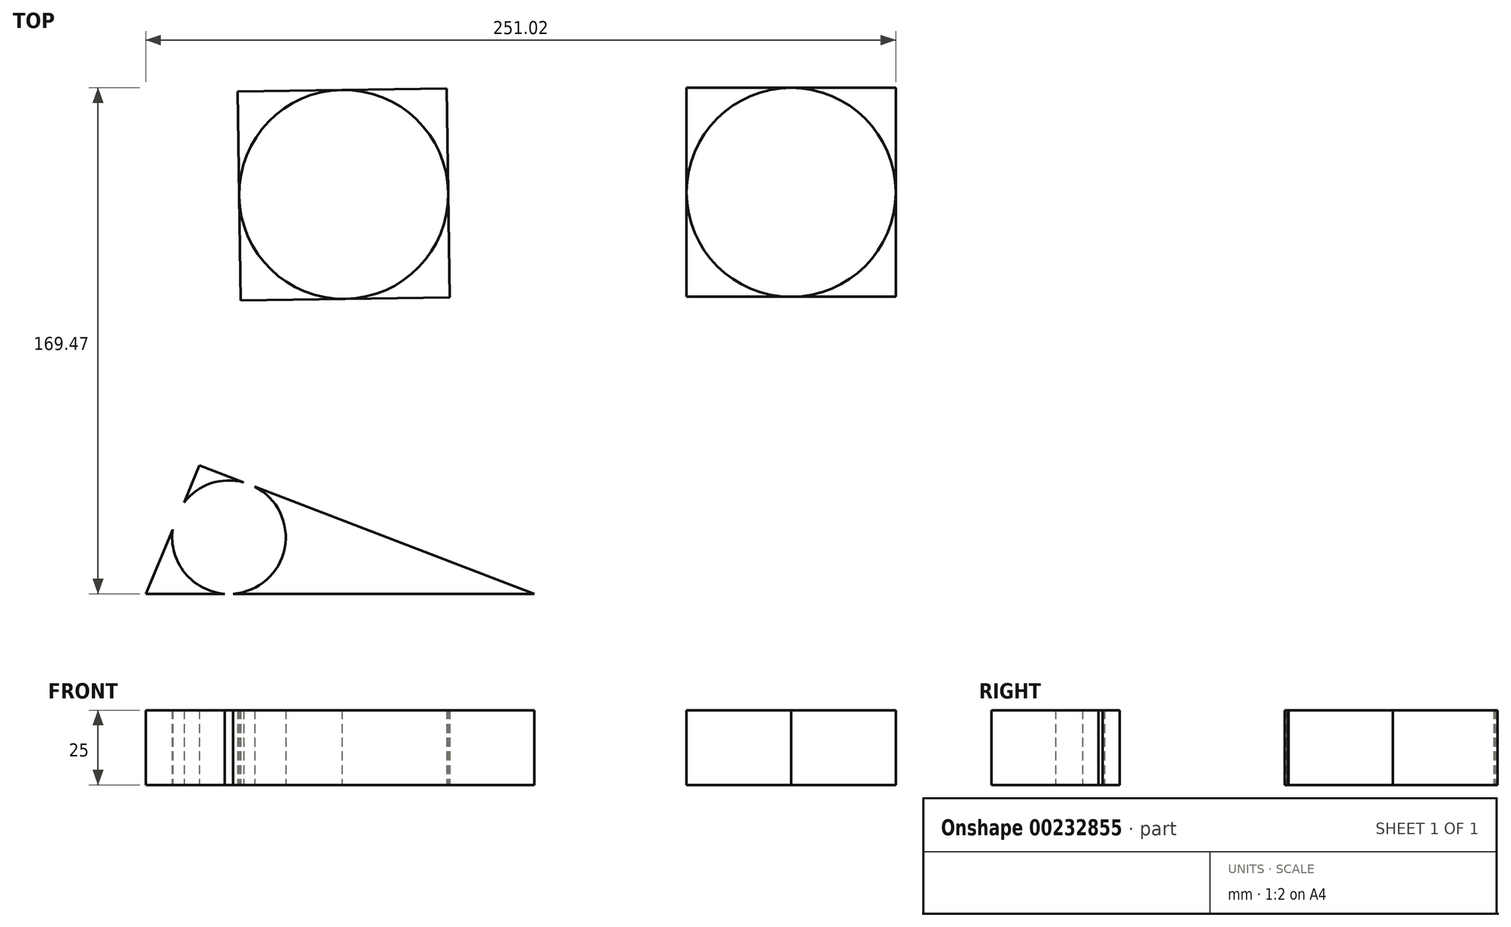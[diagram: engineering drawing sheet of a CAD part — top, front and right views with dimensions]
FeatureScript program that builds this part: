
annotation { "Feature Type Name" : "Feature", "Feature Type Description" : "" }
export const myFeature = defineFeature(function(context is Context, id is Id, definition is map)
    precondition{}
    {
        {
            var Q0;
            Q0=qCreatedBy(makeId("Top.planeOp"),FACE);
            var sketch = newSketch(context, id + "F0", { "sketchPlane" : qUnion([Q0])});
            skCircle(sketch, "E0", {"center": v(-236.28, 39.6) * mm, "radius": 35 * mm});
            skLineSegment(sketch, "E1", {"start": v(-200.74, 5.14) * mm, "end": v(-201.82, 75.14) * mm});
            skLineSegment(sketch, "E2", {"start": v(-201.82, 75.14) * mm, "end": v(-271.82, 74.06) * mm});
            skLineSegment(sketch, "E3", {"start": v(-271.82, 74.06) * mm, "end": v(-270.74, 4.07) * mm});
            skLineSegment(sketch, "E4", {"start": v(-270.74, 4.07) * mm, "end": v(-200.74, 5.14) * mm});
            skSolve(sketch);
        }
        {
            var Q0;
            {var subQ0=sQuery(id+"F0.wireOp",EDGE,"E3");Q0=makeQuery(id+"F0.imprint","IMPRINT",FACE,{"disambiguationData":[TD([[makeQuery(id+"F0.imprint","IMPRINT",EDGE,{"derivedFrom":subQ0}),1.0]])]});}
            var Q1;
            {var subQ0=sQuery(id+"F0.wireOp",EDGE,"E1");var subQ1=sQuery(id+"F0.wireOp",EDGE,"E0");var subQ2=makeQuery(id+"F0.imprint","INTERSECT",VERTEX,{"derivedFrom":[subQ1,subQ0]});Q1=makeQuery(id+"F0.imprint","IMPRINT",FACE,{"disambiguationData":[TD([[makeQuery(id+"F0.imprint","IMPRINT",EDGE,{"disambiguationData":[TD([[subQ2,-1.0]])],"derivedFrom":subQ1}),-1.0]])]});}
            extrude(context, id + "F1", {"entities" : qUnion([Q0, Q1]), "depth" : 25 * mm});
        }
        {
            var Q0;
            Q0=qCreatedBy(makeId("Top.planeOp"),FACE);
            var sketch = newSketch(context, id + "F2", { "sketchPlane" : qUnion([Q0])});
            skLineSegment(sketch, "E5", {"start": v(-121.49, 75.3) * mm, "end": v(-121.49, 5.3) * mm});
            skLineSegment(sketch, "E6", {"start": v(-121.49, 75.3) * mm, "end": v(-51.49, 75.3) * mm});
            skLineSegment(sketch, "E7", {"start": v(-51.49, 75.3) * mm, "end": v(-51.49, 5.3) * mm});
            skLineSegment(sketch, "E8", {"start": v(-51.49, 5.3) * mm, "end": v(-121.49, 5.3) * mm});
            skCircle(sketch, "E9", {"center": v(-86.49, 40.3) * mm, "radius": 35 * mm});
            skSolve(sketch);
        }
        {
            var Q0;
            {var subQ0=sQuery(id+"F2.wireOp",EDGE,"E6");var subQ1=sQuery(id+"F2.wireOp",EDGE,"E5");var subQ2=makeQuery(id+"F2.imprint","INTERSECT",VERTEX,{"derivedFrom":[subQ1,subQ0]});Q0=makeQuery(id+"F2.imprint","IMPRINT",FACE,{"disambiguationData":[TD([[makeQuery(id+"F2.imprint","IMPRINT",EDGE,{"disambiguationData":[TD([[subQ2,-1.0]])],"derivedFrom":subQ1}),1.0]])]});}
            var Q1;
            {var subQ0=sQuery(id+"F2.wireOp",EDGE,"E7");var subQ1=sQuery(id+"F2.wireOp",EDGE,"E6");var subQ2=makeQuery(id+"F2.imprint","INTERSECT",VERTEX,{"derivedFrom":[subQ1,subQ0]});Q1=makeQuery(id+"F2.imprint","IMPRINT",FACE,{"disambiguationData":[TD([[makeQuery(id+"F2.imprint","IMPRINT",EDGE,{"disambiguationData":[TD([[subQ2,1.0]])],"derivedFrom":subQ1}),-1.0]])]});}
            var Q2;
            {var subQ0=sQuery(id+"F2.wireOp",EDGE,"E8");var subQ1=sQuery(id+"F2.wireOp",EDGE,"E7");var subQ2=makeQuery(id+"F2.imprint","INTERSECT",VERTEX,{"derivedFrom":[subQ1,subQ0]});Q2=makeQuery(id+"F2.imprint","IMPRINT",FACE,{"disambiguationData":[TD([[makeQuery(id+"F2.imprint","IMPRINT",EDGE,{"disambiguationData":[TD([[subQ2,1.0]])],"derivedFrom":subQ1}),-1.0]])]});}
            var Q3;
            {var subQ0=sQuery(id+"F2.wireOp",EDGE,"E8");var subQ1=sQuery(id+"F2.wireOp",EDGE,"E5");var subQ2=makeQuery(id+"F2.imprint","INTERSECT",VERTEX,{"derivedFrom":[subQ1,subQ0]});Q3=makeQuery(id+"F2.imprint","IMPRINT",FACE,{"disambiguationData":[TD([[makeQuery(id+"F2.imprint","IMPRINT",EDGE,{"disambiguationData":[TD([[subQ2,1.0]])],"derivedFrom":subQ1}),1.0]])]});}
            extrude(context, id + "F3", {"entities" : qUnion([Q0, Q1, Q2, Q3]), "depth" : 25 * mm});
        }
        {
            var Q0;
            Q0=qCreatedBy(makeId("Top.planeOp"),FACE);
            var sketch = newSketch(context, id + "F4", { "sketchPlane" : qUnion([Q0])});
            skLineSegment(sketch, "E10", {"start": v(-302.51, -94.17) * mm, "end": v(-172.51, -94.17) * mm});
            skLineSegment(sketch, "E11", {"start": v(-172.51, -94.17) * mm, "end": v(-284.54, -51.17) * mm});
            skLineSegment(sketch, "E12", {"start": v(-284.54, -51.17) * mm, "end": v(-302.51, -94.17) * mm});
            skCircle(sketch, "E13", {"center": v(-274.69, -75.21) * mm, "radius": 19.01 * mm});
            skPoint(sketch, "E13.first.point", {"position": v(-266.12, -58.24) * mm});
            skPoint(sketch, "E13.second.point", {"position": v(-293.53, -72.67) * mm});
            skPoint(sketch, "E13.third.point", {"position": v(-273.3, -94.17) * mm});
            skSolve(sketch);
        }
        {
            var Q0;
            {var subQ0=sQuery(id+"F4.wireOp",EDGE,"E12");var subQ1=sQuery(id+"F4.wireOp",EDGE,"E10");var subQ2=makeQuery(id+"F4.imprint","INTERSECT",VERTEX,{"derivedFrom":[subQ1,subQ0]});Q0=makeQuery(id+"F4.imprint","IMPRINT",FACE,{"disambiguationData":[TD([[makeQuery(id+"F4.imprint","IMPRINT",EDGE,{"disambiguationData":[TD([[subQ2,-1.0]])],"derivedFrom":subQ1}),1.0]])]});}
            var Q1;
            {var subQ0=sQuery(id+"F4.wireOp",EDGE,"E13");var subQ1=sQuery(id+"F4.wireOp",EDGE,"E10");var subQ2=makeQuery(id+"F4.imprint","INTERSECT",VERTEX,{"disambiguationData":[OD(0.0)],"derivedFrom":[subQ1,subQ0]});Q1=makeQuery(id+"F4.imprint","IMPRINT",FACE,{"disambiguationData":[TD([[makeQuery(id+"F4.imprint","IMPRINT",EDGE,{"disambiguationData":[TD([[subQ2,-1.0]])],"derivedFrom":subQ1}),-1.0]])]});}
            var Q2;
            {var subQ0=sQuery(id+"F4.wireOp",EDGE,"E13");var subQ1=sQuery(id+"F4.wireOp",EDGE,"E11");var subQ2=makeQuery(id+"F4.imprint","INTERSECT",VERTEX,{"disambiguationData":[OD(0.0)],"derivedFrom":[subQ1,subQ0]});Q2=makeQuery(id+"F4.imprint","IMPRINT",FACE,{"disambiguationData":[TD([[makeQuery(id+"F4.imprint","IMPRINT",EDGE,{"disambiguationData":[TD([[subQ2,-1.0]])],"derivedFrom":subQ1}),-1.0]])]});}
            var Q3;
            {var subQ0=sQuery(id+"F4.wireOp",EDGE,"E12");var subQ1=sQuery(id+"F4.wireOp",EDGE,"E11");var subQ2=makeQuery(id+"F4.imprint","INTERSECT",VERTEX,{"derivedFrom":[subQ1,subQ0]});Q3=makeQuery(id+"F4.imprint","IMPRINT",FACE,{"disambiguationData":[TD([[makeQuery(id+"F4.imprint","IMPRINT",EDGE,{"disambiguationData":[TD([[subQ2,1.0]])],"derivedFrom":subQ1}),1.0]])]});}
            var Q4;
            {var subQ0=sQuery(id+"F4.wireOp",EDGE,"E13");var subQ1=sQuery(id+"F4.wireOp",EDGE,"E12");var subQ2=makeQuery(id+"F4.imprint","INTERSECT",VERTEX,{"disambiguationData":[OD(0.0)],"derivedFrom":[subQ1,subQ0]});Q4=makeQuery(id+"F4.imprint","IMPRINT",FACE,{"disambiguationData":[TD([[makeQuery(id+"F4.imprint","IMPRINT",EDGE,{"disambiguationData":[TD([[subQ2,-1.0]])],"derivedFrom":subQ1}),-1.0]])]});}
            var Q5;
            {var subQ0=sQuery(id+"F4.wireOp",EDGE,"E11");var subQ1=sQuery(id+"F4.wireOp",EDGE,"E10");var subQ2=makeQuery(id+"F4.imprint","INTERSECT",VERTEX,{"derivedFrom":[subQ1,subQ0]});Q5=makeQuery(id+"F4.imprint","IMPRINT",FACE,{"disambiguationData":[TD([[makeQuery(id+"F4.imprint","IMPRINT",EDGE,{"disambiguationData":[TD([[subQ2,1.0]])],"derivedFrom":subQ1}),1.0]])]});}
            extrude(context, id + "F5", {"entities" : qUnion([Q0, Q1, Q2, Q3, Q4, Q5]), "depth" : 25 * mm});
        }
    });
